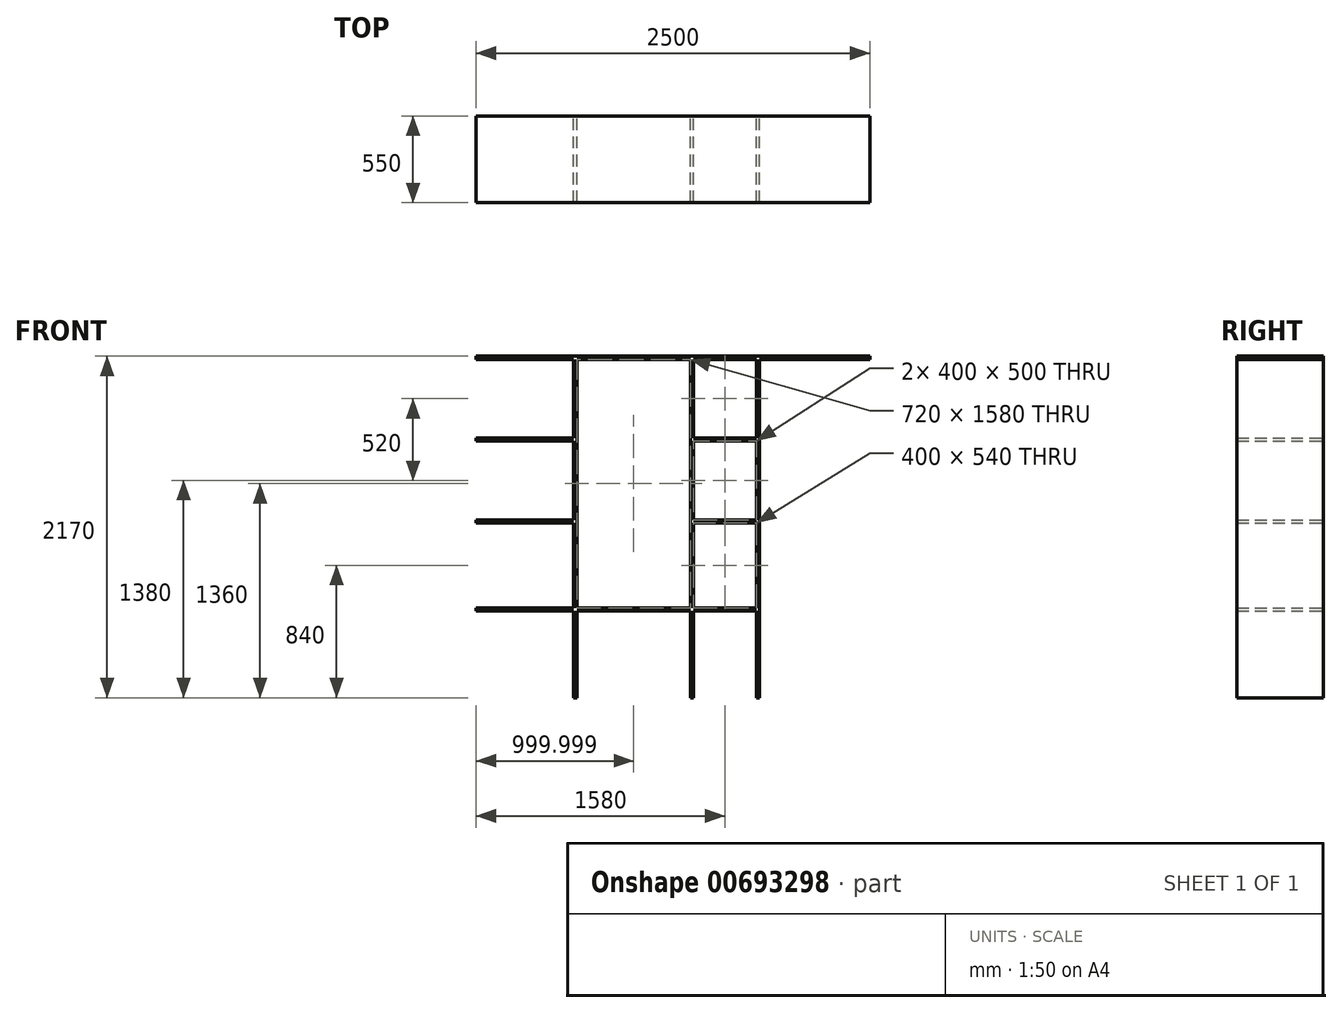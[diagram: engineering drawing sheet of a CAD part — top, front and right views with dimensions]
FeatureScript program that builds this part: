
annotation { "Feature Type Name" : "Feature", "Feature Type Description" : "" }
export const myFeature = defineFeature(function(context is Context, id is Id, definition is map)
    precondition{}
    {
        {
            var Q0;
            Q0=qCreatedBy(makeId("Front.planeOp"),FACE);
            var sketch = newSketch(context, id + "F0", { "sketchPlane" : qUnion([Q0])});
            skLineSegment(sketch, "E0.bottom", {"start": v(-914.81, 520) * mm, "end": v(1585.19, 520) * mm});
            skLineSegment(sketch, "E0.top", {"start": v(-914.81, 500) * mm, "end": v(1585.19, 500) * mm});
            skLineSegment(sketch, "E0.left", {"start": v(-914.81, 520) * mm, "end": v(-914.81, 500) * mm});
            skLineSegment(sketch, "E0.right", {"start": v(1585.19, 520) * mm, "end": v(1585.19, 500) * mm});
            skLineSegment(sketch, "E1.bottom", {"start": v(-294.81, 500) * mm, "end": v(-274.81, 500) * mm});
            skLineSegment(sketch, "E1.top", {"start": v(-294.81, -1650) * mm, "end": v(-274.81, -1650) * mm});
            skLineSegment(sketch, "E1.left", {"start": v(-294.81, 500) * mm, "end": v(-294.81, -1650) * mm});
            skLineSegment(sketch, "E1.right", {"start": v(-274.81, 500) * mm, "end": v(-274.81, -1650) * mm});
            skLineSegment(sketch, "E2.bottom", {"start": v(445.19, 500) * mm, "end": v(465.19, 500) * mm});
            skLineSegment(sketch, "E2.top", {"start": v(445.19, -1650) * mm, "end": v(465.19, -1650) * mm});
            skLineSegment(sketch, "E2.left", {"start": v(445.19, 500) * mm, "end": v(445.19, -1650) * mm});
            skLineSegment(sketch, "E2.right", {"start": v(465.19, 500) * mm, "end": v(465.19, -1650) * mm});
            skLineSegment(sketch, "E3.bottom", {"start": v(865.19, 500) * mm, "end": v(885.19, 500) * mm});
            skLineSegment(sketch, "E3.top", {"start": v(865.19, -1650) * mm, "end": v(885.19, -1650) * mm});
            skLineSegment(sketch, "E3.left", {"start": v(865.19, 500) * mm, "end": v(865.19, -1650) * mm});
            skLineSegment(sketch, "E3.right", {"start": v(885.19, 500) * mm, "end": v(885.19, -1650) * mm});
            skLineSegment(sketch, "E4.bottom", {"start": v(-294.81, -20) * mm, "end": v(-914.81, -20) * mm});
            skLineSegment(sketch, "E4.top", {"start": v(-294.81, 0) * mm, "end": v(-914.81, 0) * mm});
            skLineSegment(sketch, "E4.left", {"start": v(-294.81, -20) * mm, "end": v(-294.81, 0) * mm});
            skLineSegment(sketch, "E4.right", {"start": v(-914.81, -20) * mm, "end": v(-914.81, 0) * mm});
            skLineSegment(sketch, "E5.bottom", {"start": v(-294.81, -540) * mm, "end": v(-914.81, -540) * mm});
            skLineSegment(sketch, "E5.top", {"start": v(-294.81, -520) * mm, "end": v(-914.81, -520) * mm});
            skLineSegment(sketch, "E5.left", {"start": v(-294.81, -540) * mm, "end": v(-294.81, -520) * mm});
            skLineSegment(sketch, "E5.right", {"start": v(-914.81, -540) * mm, "end": v(-914.81, -520) * mm});
            skLineSegment(sketch, "E6.bottom", {"start": v(-294.81, -1100) * mm, "end": v(-914.81, -1100) * mm});
            skLineSegment(sketch, "E6.top", {"start": v(-294.81, -1080) * mm, "end": v(-914.81, -1080) * mm});
            skLineSegment(sketch, "E6.left", {"start": v(-294.81, -1100) * mm, "end": v(-294.81, -1080) * mm});
            skLineSegment(sketch, "E6.right", {"start": v(-914.81, -1100) * mm, "end": v(-914.81, -1080) * mm});
            skLineSegment(sketch, "E7.bottom", {"start": v(-274.81, -1080) * mm, "end": v(445.19, -1080) * mm});
            skLineSegment(sketch, "E7.top", {"start": v(-274.81, -1100) * mm, "end": v(445.19, -1100) * mm});
            skLineSegment(sketch, "E7.left", {"start": v(-274.81, -1080) * mm, "end": v(-274.81, -1100) * mm});
            skLineSegment(sketch, "E7.right", {"start": v(445.19, -1080) * mm, "end": v(445.19, -1100) * mm});
            skLineSegment(sketch, "E8.bottom", {"start": v(465.19, -1080) * mm, "end": v(865.19, -1080) * mm});
            skLineSegment(sketch, "E8.top", {"start": v(465.19, -1100) * mm, "end": v(865.19, -1100) * mm});
            skLineSegment(sketch, "E8.left", {"start": v(465.19, -1080) * mm, "end": v(465.19, -1100) * mm});
            skLineSegment(sketch, "E8.right", {"start": v(865.19, -1080) * mm, "end": v(865.19, -1100) * mm});
            skLineSegment(sketch, "E9.bottom", {"start": v(465.19, -540) * mm, "end": v(865.19, -540) * mm});
            skLineSegment(sketch, "E9.top", {"start": v(465.19, -520) * mm, "end": v(865.19, -520) * mm});
            skLineSegment(sketch, "E9.left", {"start": v(465.19, -540) * mm, "end": v(465.19, -520) * mm});
            skLineSegment(sketch, "E9.right", {"start": v(865.19, -540) * mm, "end": v(865.19, -520) * mm});
            skLineSegment(sketch, "E10.bottom", {"start": v(465.19, -20) * mm, "end": v(865.19, -20) * mm});
            skLineSegment(sketch, "E10.top", {"start": v(465.19, 0) * mm, "end": v(865.19, 0) * mm});
            skLineSegment(sketch, "E10.left", {"start": v(465.19, -20) * mm, "end": v(465.19, 0) * mm});
            skLineSegment(sketch, "E10.right", {"start": v(865.19, -20) * mm, "end": v(865.19, 0) * mm});
            skSolve(sketch);
        }
        {
            var Q0;
            Q0 = qSketchRegion(id + "F0", true);
            var Q1;
            Q1=makeQuery(id+"F0.imprint","IMPRINT",FACE,{"disambiguationData":[TD([[makeQuery(id+"F0.imprint","IMPRINT",EDGE,{"derivedFrom":sQuery(id+"F0.wireOp",EDGE,"E10.bottom")}),1.0]])]});
            var Q2;
            Q2=makeQuery(id+"F0.imprint","IMPRINT",FACE,{"disambiguationData":[TD([[makeQuery(id+"F0.imprint","IMPRINT",EDGE,{"derivedFrom":sQuery(id+"F0.wireOp",EDGE,"E9.bottom")}),1.0]])]});
            extrude(context, id + "F1", {"entities" : qUnion([Q0, Q1, Q2]), "depth" : 550 * mm, "offsetDistance" : 25 * mm});
        }
    });
